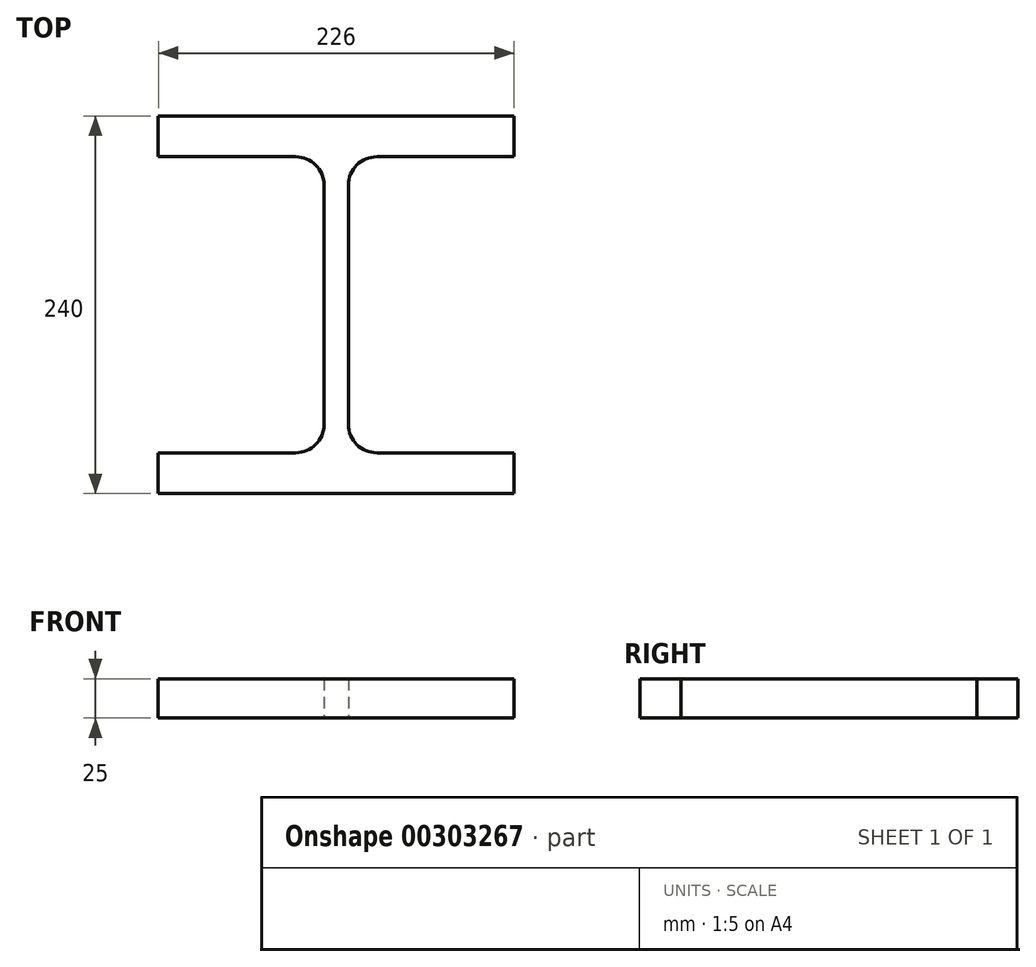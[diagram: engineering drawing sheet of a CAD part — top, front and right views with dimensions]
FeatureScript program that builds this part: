
annotation { "Feature Type Name" : "Feature", "Feature Type Description" : "" }
export const myFeature = defineFeature(function(context is Context, id is Id, definition is map)
    precondition{}
    {
        {
            var Q0;
            Q0=qCreatedBy(makeId("Top.planeOp"),FACE);
            var sketch = newSketch(context, id + "F0", { "sketchPlane" : qUnion([Q0])});
            skLineSegment(sketch, "E0", {"start": v(-58.88, 162.14) * mm, "end": v(-58.88, 136.14) * mm});
            skLineSegment(sketch, "E1", {"start": v(-58.88, -77.86) * mm, "end": v(167.12, -77.86) * mm});
            skLineSegment(sketch, "E2", {"start": v(167.12, -77.86) * mm, "end": v(167.12, -51.86) * mm});
            skLineSegment(sketch, "E3", {"start": v(167.12, 162.14) * mm, "end": v(-58.88, 162.14) * mm});
            skPoint(sketch, "E4.endSnap0", {"position": v(54.12, 42.14) * mm});
            skLineSegment(sketch, "E5", {"start": v(167.12, -51.86) * mm, "end": v(79.87, -51.86) * mm});
            skLineSegment(sketch, "E6", {"start": v(167.12, 162.14) * mm, "end": v(167.12, 136.14) * mm});
            skLineSegment(sketch, "E7", {"start": v(167.12, 136.14) * mm, "end": v(79.87, 136.14) * mm});
            skLineSegment(sketch, "E8", {"start": v(61.87, 42.14) * mm, "end": v(61.87, 118.14) * mm});
            skLineSegment(sketch, "E9", {"start": v(61.87, 42.14) * mm, "end": v(61.87, -33.86) * mm});
            skLineSegment(sketch, "E10", {"start": v(46.37, 42.14) * mm, "end": v(46.37, 118.14) * mm});
            skLineSegment(sketch, "E11", {"start": v(46.37, 42.14) * mm, "end": v(46.37, -33.86) * mm});
            skPoint(sketch, "E11.endSnap0", {"position": v(54.12, -51.86) * mm});
            skPoint(sketch, "E12.start.orphan", {"position": v(54.12, -77.86) * mm});
            skLineSegment(sketch, "E13.trimOffspring", {"start": v(28.37, -51.86) * mm, "end": v(-58.88, -51.86) * mm});
            skPoint(sketch, "E4.start.orphan", {"position": v(54.12, 42.14) * mm});
            skPoint(sketch, "E14.trimOffspring.end.orphan", {"position": v(54.12, 162.14) * mm});
            skLineSegment(sketch, "E15.trimOffspring", {"start": v(28.37, 136.14) * mm, "end": v(-58.88, 136.14) * mm});
            skLineSegment(sketch, "E16.trimOffspring", {"start": v(167.12, 136.14) * mm, "end": v(167.12, 162.14) * mm});
            skLineSegment(sketch, "E17.trimOffspring", {"start": v(-58.88, -51.86) * mm, "end": v(-58.88, -77.86) * mm});
            skPoint(sketch, "E18.visualSharp", {"position": v(46.37, -51.86) * mm});
            skArc(sketch, "E18.filletArc", {"start": v(28.37, -51.86) * mm, "mid": v(41.1, -46.59) * mm, "end": v(46.37, -33.86) * mm});
            skPoint(sketch, "E19.visualSharp", {"position": v(61.87, -51.86) * mm});
            skArc(sketch, "E19.filletArc", {"start": v(61.87, -33.86) * mm, "mid": v(67.14, -46.59) * mm, "end": v(79.87, -51.86) * mm});
            skPoint(sketch, "E20.visualSharp", {"position": v(61.87, 136.14) * mm});
            skArc(sketch, "E20.filletArc", {"start": v(79.87, 136.14) * mm, "mid": v(67.14, 130.87) * mm, "end": v(61.87, 118.14) * mm});
            skPoint(sketch, "E21.visualSharp", {"position": v(46.37, 136.14) * mm});
            skArc(sketch, "E21.filletArc", {"start": v(46.37, 118.14) * mm, "mid": v(41.1, 130.87) * mm, "end": v(28.37, 136.14) * mm});
            skSolve(sketch);
        }
        {
            var Q0;
            Q0=makeQuery(id+"F0.imprint","IMPRINT",FACE,{"disambiguationData":[TD([[makeQuery(id+"F0.imprint","IMPRINT",EDGE,{"derivedFrom":sQuery(id+"F0.wireOp",EDGE,"E0")}),1.0]])]});
            extrude(context, id + "F1", {"entities" : qUnion([Q0]), "depth" : 25 * mm});
        }
    });
